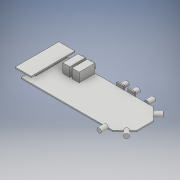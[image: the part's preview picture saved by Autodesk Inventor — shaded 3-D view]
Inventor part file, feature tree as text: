
AUTODESK INVENTOR PART (.ipt)
format: ipt  version: 2018 (Build 220112000, 112)  size: 247,808 bytes
history: native  units: mm
features: extrude x12, sketch x12
ambient origin geometry x8: Origin, YZ Plane, XZ Plane, XY Plane, X Axis, Y Axis, Z Axis, Center Point
bodies: Solid1 (feature_tree)
feature tree (24):
  extrude  "Extrusion1"  Depth=142.0mm
  extrude  "Extrusion2"  Depth=55.7mm
  extrude  "Extrusion3"  Depth=9.6mm
  extrude  "Extrusion4"  Depth=84.85mm
  extrude  "Extrusion5"  Depth=4.4mm TaperAngle=0.0deg
  extrude  "Extrusion6"  Depth=3.67mm
  extrude  "Extrusion7"  Depth=12.6mm
  extrude  "Extrusion8"  Depth=9.5mm TaperAngle=0.0deg
  extrude  "Extrusion9"  Depth=9.5mm TaperAngle=0.0deg
  extrude  "Extrusion10"  Depth=9.5mm
  extrude  "Extrusion11"  Depth=9.5mm TaperAngle=0.0deg
  extrude  "Extrusion12"  Depth=1.55mm
  sketch  "Sketch1"  dims[d0=1.6mm d1=0.0mm d2=142.0mm]
  sketch  "Sketch2"  dims[d3=55.7mm d4=23.6mm]
  sketch  "Sketch3"  dims[d5=23.0mm d6=9.6mm]
  sketch  "Sketch4"  dims[d7=1.5mm d8=84.85mm]
  sketch  "Sketch5"  dims[d9=100.0mm d10=4.4mm d11=0.0mm]
  sketch  "Sketch6"  dims[d12=3.67mm d13=0.0mm d14=6.23mm]
  sketch  "Sketch7"  dims[d15=8.0mm d16=0.0mm d17=12.6mm]
  sketch  "Sketch8"  dims[d18=6.22mm d19=9.5mm d20=0.0mm]
  sketch  "Sketch9"  dims[d22=6.2mm d23=9.5mm d24=0.0mm]
  sketch  "Sketch10"  dims[d25=9.5mm d26=9.0mm]
  sketch  "Sketch11"  dims[d27=6.25mm d28=9.5mm d29=0.0mm]
  sketch  "Sketch12"  dims[d30=6.25mm d31=9.0mm d32=9.5mm d33=0.0mm d34=9.75mm d35=21.0mm d36=1.21mm d37=23.5mm d38=36.25mm d39=12.6mm d40=0.0mm d41=5.6mm d42=5.6mm d43=8.9mm d44=2.54mm d45=0.0mm d46=5.6mm d47=42.6mm d48=1.7mm d49=2.8mm d50=4.15mm d51=0.0mm d52=22.1mm d53=60.0mm d54=8.6mm d55=13.75mm d56=1.55mm d57=0.0mm]
